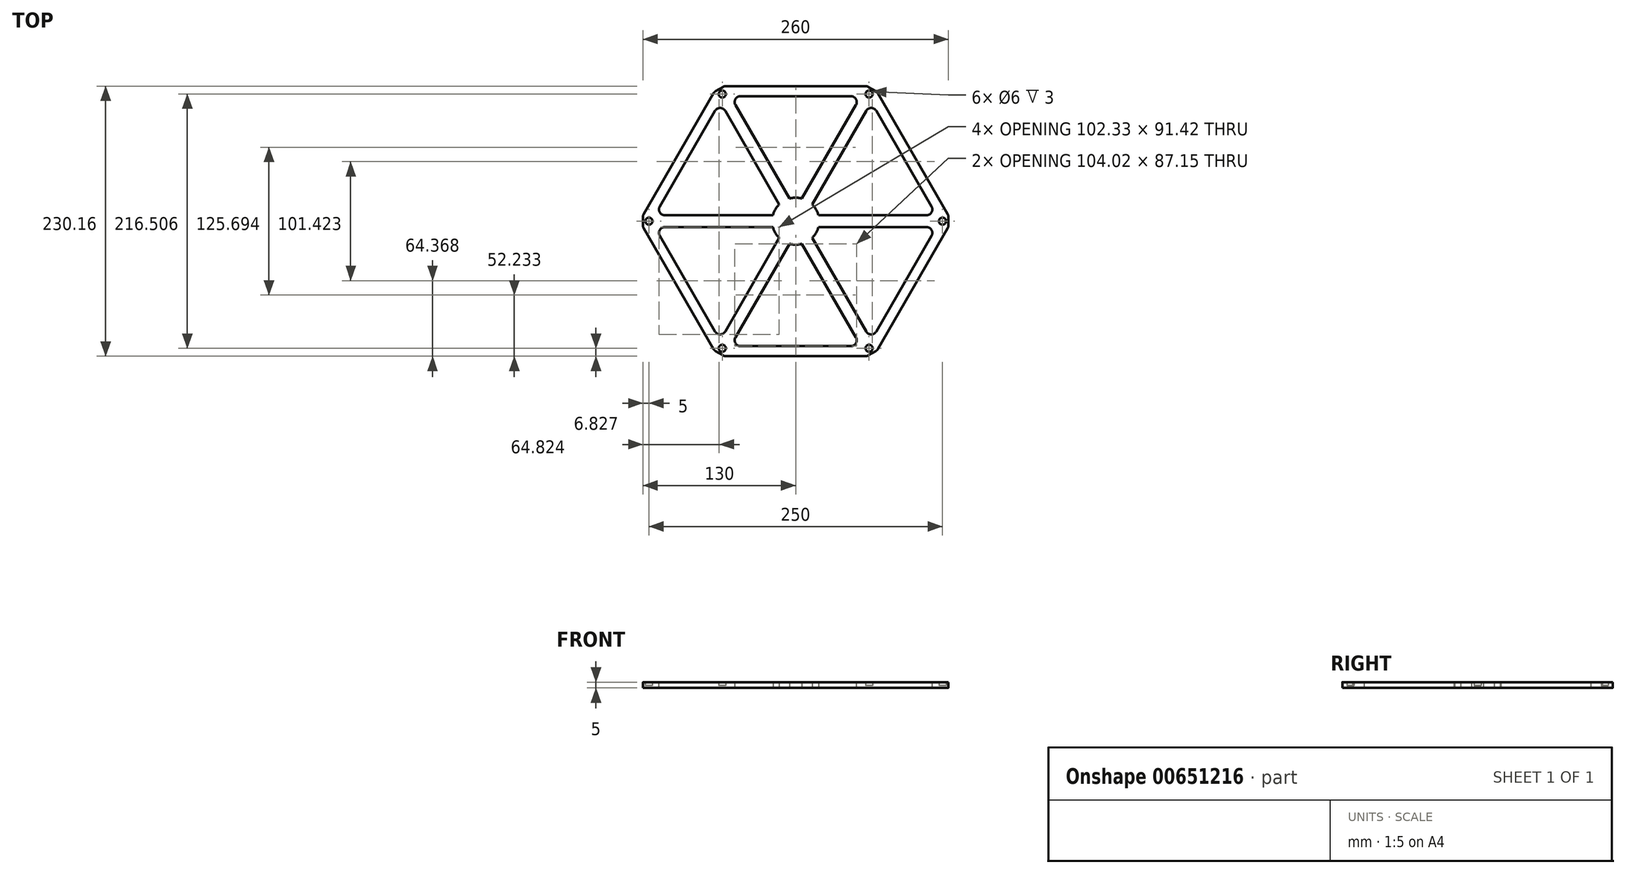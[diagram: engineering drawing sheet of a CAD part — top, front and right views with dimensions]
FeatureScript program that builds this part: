
annotation { "Feature Type Name" : "Feature", "Feature Type Description" : "" }
export const myFeature = defineFeature(function(context is Context, id is Id, definition is map)
    precondition{}
    {
        {
            var Q0;
            Q0=qCreatedBy(makeId("Top.planeOp"),FACE);
            var sketch = newSketch(context, id + "F0", { "sketchPlane" : qUnion([Q0])});
            skCircle(sketch, "E0", {"center": v(0, 0) * mm, "radius": 20 * mm});
            skLineSegment(sketch, "E1", {"start": v(-20, 0) * mm, "end": v(20, 0) * mm, "construction": true});
            skLineSegment(sketch, "E2", {"start": v(0, 0) * mm, "end": v(-10, 17.32) * mm, "construction": true});
            skLineSegment(sketch, "E3", {"start": v(0, 0) * mm, "end": v(10, 17.32) * mm, "construction": true});
            skLineSegment(sketch, "E4", {"start": v(0, 0) * mm, "end": v(-10, -17.32) * mm, "construction": true});
            skLineSegment(sketch, "E5", {"start": v(0, 0) * mm, "end": v(10, -17.32) * mm, "construction": true});
            skLineSegment(sketch, "E6", {"start": v(-20, 0) * mm, "end": v(-120, 0) * mm, "construction": true});
            skLineSegment(sketch, "E7", {"start": v(-10, 17.32) * mm, "end": v(-60, 103.92) * mm, "construction": true});
            skLineSegment(sketch, "E8", {"start": v(10, 17.32) * mm, "end": v(60, 103.92) * mm, "construction": true});
            skLineSegment(sketch, "E9", {"start": v(20, 0) * mm, "end": v(120, 0) * mm, "construction": true});
            skLineSegment(sketch, "E10", {"start": v(10, -17.32) * mm, "end": v(60, -103.92) * mm, "construction": true});
            skLineSegment(sketch, "E11", {"start": v(-10, -17.32) * mm, "end": v(-60, -103.92) * mm, "construction": true});
            skLineSegment(sketch, "E12", {"start": v(-120, 5) * mm, "end": v(-19.36, 5) * mm});
            skLineSegment(sketch, "E13", {"start": v(-120, -5) * mm, "end": v(-19.36, -5) * mm});
            skLineSegment(sketch, "E14.1.1", {"start": v(-64.33, -101.42) * mm, "end": v(-14.01, -14.27) * mm});
            skLineSegment(sketch, "E14.1.2", {"start": v(-55.67, -106.42) * mm, "end": v(-5.35, -19.27) * mm});
            skLineSegment(sketch, "E14.2.1", {"start": v(55.67, -106.42) * mm, "end": v(5.35, -19.27) * mm});
            skLineSegment(sketch, "E14.2.2", {"start": v(64.33, -101.42) * mm, "end": v(14.01, -14.27) * mm});
            skLineSegment(sketch, "E14.3.1", {"start": v(120, -5) * mm, "end": v(19.36, -5) * mm});
            skLineSegment(sketch, "E14.3.2", {"start": v(120, 5) * mm, "end": v(19.36, 5) * mm});
            skLineSegment(sketch, "E14.4.1", {"start": v(64.33, 101.42) * mm, "end": v(14.01, 14.27) * mm});
            skLineSegment(sketch, "E14.4.2", {"start": v(55.67, 106.42) * mm, "end": v(5.35, 19.27) * mm});
            skLineSegment(sketch, "E14.5.1", {"start": v(-55.67, 106.42) * mm, "end": v(-5.35, 19.27) * mm});
            skLineSegment(sketch, "E14.5.2", {"start": v(-64.33, 101.42) * mm, "end": v(-14.01, 14.27) * mm});
            skLineSegment(sketch, "E15", {"start": v(-64.33, 101.42) * mm, "end": v(-60, 103.92) * mm});
            skLineSegment(sketch, "E16", {"start": v(-55.67, 106.42) * mm, "end": v(-60, 103.92) * mm});
            skLineSegment(sketch, "E17", {"start": v(55.67, 106.42) * mm, "end": v(60, 103.92) * mm});
            skLineSegment(sketch, "E18", {"start": v(64.33, 101.42) * mm, "end": v(60, 103.92) * mm});
            skLineSegment(sketch, "E19", {"start": v(120, 5) * mm, "end": v(120, -5) * mm});
            skLineSegment(sketch, "E20", {"start": v(64.33, -101.42) * mm, "end": v(55.67, -106.42) * mm});
            skLineSegment(sketch, "E21", {"start": v(-55.67, -106.42) * mm, "end": v(-64.33, -101.42) * mm});
            skLineSegment(sketch, "E22", {"start": v(-120, -5) * mm, "end": v(-120, 5) * mm});
            skLineSegment(sketch, "E23", {"start": v(-64.33, 101.42) * mm, "end": v(-120, 5) * mm});
            skLineSegment(sketch, "E24", {"start": v(-120, -5) * mm, "end": v(-64.33, -101.42) * mm});
            skLineSegment(sketch, "E25", {"start": v(-55.67, -106.42) * mm, "end": v(55.67, -106.42) * mm});
            skLineSegment(sketch, "E26", {"start": v(64.33, -101.42) * mm, "end": v(120, -5) * mm});
            skLineSegment(sketch, "E27", {"start": v(64.33, 101.42) * mm, "end": v(120, 5) * mm});
            skLineSegment(sketch, "E28", {"start": v(-55.67, 106.42) * mm, "end": v(55.67, 106.42) * mm});
            skLineSegment(sketch, "E29", {"start": v(-120, 0) * mm, "end": v(-130, 0) * mm, "construction": true});
            skLineSegment(sketch, "E30", {"start": v(-60, 103.92) * mm, "end": v(-65, 112.58) * mm, "construction": true});
            skLineSegment(sketch, "E31", {"start": v(60, 103.92) * mm, "end": v(65, 112.58) * mm, "construction": true});
            skLineSegment(sketch, "E32", {"start": v(120, 0) * mm, "end": v(130, 0) * mm, "construction": true});
            skLineSegment(sketch, "E33", {"start": v(60, -103.92) * mm, "end": v(65.05, -112.56) * mm, "construction": true});
            skLineSegment(sketch, "E34", {"start": v(-60, -103.92) * mm, "end": v(-65, -112.58) * mm, "construction": true});
            skLineSegment(sketch, "E35", {"start": v(-65, 112.58) * mm, "end": v(-60.67, 115.08) * mm});
            skLineSegment(sketch, "E36", {"start": v(-65, 112.58) * mm, "end": v(-69.33, 110.08) * mm});
            skLineSegment(sketch, "E37.1.0", {"start": v(-130, 0) * mm, "end": v(-130, -5) * mm});
            skLineSegment(sketch, "E37.1.1", {"start": v(-130, 0) * mm, "end": v(-130, 5) * mm});
            skLineSegment(sketch, "E37.2.0", {"start": v(-65, -112.58) * mm, "end": v(-60.67, -115.08) * mm});
            skLineSegment(sketch, "E37.2.1", {"start": v(-65, -112.58) * mm, "end": v(-69.33, -110.08) * mm});
            skLineSegment(sketch, "E37.3.0", {"start": v(65, -112.58) * mm, "end": v(69.33, -110.08) * mm});
            skLineSegment(sketch, "E37.3.1", {"start": v(65, -112.58) * mm, "end": v(60.67, -115.08) * mm});
            skLineSegment(sketch, "E37.4.0", {"start": v(130, 0) * mm, "end": v(130, 5) * mm});
            skLineSegment(sketch, "E37.4.1", {"start": v(130, 0) * mm, "end": v(130, -5) * mm});
            skLineSegment(sketch, "E37.5.0", {"start": v(65, 112.58) * mm, "end": v(60.67, 115.08) * mm});
            skLineSegment(sketch, "E37.5.1", {"start": v(65, 112.58) * mm, "end": v(69.33, 110.08) * mm});
            skLineSegment(sketch, "E38", {"start": v(-69.33, 110.08) * mm, "end": v(-130, 5) * mm});
            skLineSegment(sketch, "E39", {"start": v(-130, -5) * mm, "end": v(-69.33, -110.08) * mm});
            skLineSegment(sketch, "E40", {"start": v(-60.67, -115.08) * mm, "end": v(60.67, -115.08) * mm});
            skLineSegment(sketch, "E41", {"start": v(69.33, -110.08) * mm, "end": v(130, -5) * mm});
            skLineSegment(sketch, "E42", {"start": v(130, 5) * mm, "end": v(69.33, 110.08) * mm});
            skLineSegment(sketch, "E43", {"start": v(60.67, 115.08) * mm, "end": v(-60.67, 115.08) * mm});
            skLineSegment(sketch, "E44", {"start": v(60.67, 115.08) * mm, "end": v(64.33, 101.42) * mm, "construction": true});
            skLineSegment(sketch, "E45", {"start": v(55.67, 106.42) * mm, "end": v(69.33, 110.08) * mm, "construction": true});
            skPoint(sketch, "E46", {"position": v(62.5, 108.25) * mm});
            skCircle(sketch, "E47", {"center": v(62.5, 108.25) * mm, "radius": 3 * mm});
            skCircle(sketch, "E48.1.0", {"center": v(-62.5, 108.25) * mm, "radius": 3 * mm});
            skCircle(sketch, "E48.2.0", {"center": v(-125, 0) * mm, "radius": 3 * mm});
            skCircle(sketch, "E48.3.0", {"center": v(-62.5, -108.25) * mm, "radius": 3 * mm});
            skCircle(sketch, "E48.4.0", {"center": v(62.5, -108.25) * mm, "radius": 3 * mm});
            skCircle(sketch, "E48.5.0", {"center": v(125, 0) * mm, "radius": 3 * mm});
            skSolve(sketch);
        }
        {
            var Q0;
            Q0=makeQuery(id+"F0.imprint","IMPRINT",FACE,{"disambiguationData":[TD([[makeQuery(id+"F0.imprint","IMPRINT",EDGE,{"derivedFrom":sQuery(id+"F0.wireOp",EDGE,"E15")}),1.0]])]});
            extrude(context, id + "F1", {"entities" : qUnion([Q0]), "depth" : 5 * mm, "offsetDistance" : 25 * mm});
        }
        {
            var Q0;
            {var subQ0=sQuery(id+"F0.wireOp",EDGE,"E0");var subQ8=makeQuery(id+"F0.imprint","INTERSECT",VERTEX,{"derivedFrom":[subQ0,sQuery(id+"F0.wireOp",EDGE,"E14.3.2")]});Q0=makeQuery(id+"F0.imprint","IMPRINT",FACE,{"disambiguationData":[TD([[makeQuery(id+"F0.imprint","IMPRINT",EDGE,{"disambiguationData":[TD([[subQ8,-1.0]])],"derivedFrom":subQ0}),1.0]])]});}
            var Q1;
            {var subQ0=sQuery(id+"F0.wireOp",EDGE,"E12");Q1=makeQuery(id+"F0.imprint","IMPRINT",FACE,{"disambiguationData":[TD([[makeQuery(id+"F0.imprint","IMPRINT",EDGE,{"derivedFrom":subQ0}),-1.0]])]});}
            var Q2;
            {var subQ0=sQuery(id+"F0.wireOp",EDGE,"E14.5.1");Q2=makeQuery(id+"F0.imprint","IMPRINT",FACE,{"disambiguationData":[TD([[makeQuery(id+"F0.imprint","IMPRINT",EDGE,{"derivedFrom":subQ0}),-1.0]])]});}
            var Q3;
            {var subQ0=sQuery(id+"F0.wireOp",EDGE,"E14.4.1");Q3=makeQuery(id+"F0.imprint","IMPRINT",FACE,{"disambiguationData":[TD([[makeQuery(id+"F0.imprint","IMPRINT",EDGE,{"derivedFrom":subQ0}),-1.0]])]});}
            var Q4;
            {var subQ0=sQuery(id+"F0.wireOp",EDGE,"E14.3.1");Q4=makeQuery(id+"F0.imprint","IMPRINT",FACE,{"disambiguationData":[TD([[makeQuery(id+"F0.imprint","IMPRINT",EDGE,{"derivedFrom":subQ0}),-1.0]])]});}
            var Q5;
            {var subQ0=sQuery(id+"F0.wireOp",EDGE,"E14.2.1");Q5=makeQuery(id+"F0.imprint","IMPRINT",FACE,{"disambiguationData":[TD([[makeQuery(id+"F0.imprint","IMPRINT",EDGE,{"derivedFrom":subQ0}),-1.0]])]});}
            var Q6;
            {var subQ0=sQuery(id+"F0.wireOp",EDGE,"E14.1.1");Q6=makeQuery(id+"F0.imprint","IMPRINT",FACE,{"disambiguationData":[TD([[makeQuery(id+"F0.imprint","IMPRINT",EDGE,{"derivedFrom":subQ0}),-1.0]])]});}
            extrude(context, id + "F2", {"entities" : qUnion([Q0, Q1, Q2, Q3, Q4, Q5, Q6]), "operationType" : NewBodyOperationType.ADD, "depth" : 5 * mm, "offsetDistance" : 25 * mm});
        }
        {
            var Q0;
            Q0=makeQuery(id+"F1.opExtrude","SWEPT_EDGE",EDGE,{"disambiguationData":[OSD([sQuery(id+"F0.wireOp",EDGE,"E37.2.0"),sQuery(id+"F0.wireOp",EDGE,"E40")])]});
            fillet(context, id + "F3", {"entities" : qUnion([Q0]), "radius" : 5 * mm, "tangentPropagation" : true, "allowEdgeOverflow" : false});
        }
        {
            var Q0;
            Q0=makeQuery(id+"F1.opExtrude","SWEPT_EDGE",EDGE,{"disambiguationData":[OSD([sQuery(id+"F0.wireOp",EDGE,"E37.2.1"),sQuery(id+"F0.wireOp",EDGE,"E39")])]});
            var Q1;
            Q1=makeQuery(id+"F1.opExtrude","SWEPT_EDGE",EDGE,{"disambiguationData":[OSD([sQuery(id+"F0.wireOp",EDGE,"E37.3.1"),sQuery(id+"F0.wireOp",EDGE,"E40")])]});
            var Q2;
            Q2=makeQuery(id+"F1.opExtrude","SWEPT_EDGE",EDGE,{"disambiguationData":[OSD([sQuery(id+"F0.wireOp",EDGE,"E37.3.0"),sQuery(id+"F0.wireOp",EDGE,"E41")])]});
            var Q3;
            Q3=makeQuery(id+"F1.opExtrude","SWEPT_EDGE",EDGE,{"disambiguationData":[OSD([sQuery(id+"F0.wireOp",EDGE,"E37.4.1"),sQuery(id+"F0.wireOp",EDGE,"E41")])]});
            var Q4;
            Q4=makeQuery(id+"F1.opExtrude","SWEPT_EDGE",EDGE,{"disambiguationData":[OSD([sQuery(id+"F0.wireOp",EDGE,"E37.4.0"),sQuery(id+"F0.wireOp",EDGE,"E42")])]});
            var Q5;
            Q5=makeQuery(id+"F1.opExtrude","SWEPT_EDGE",EDGE,{"disambiguationData":[OSD([sQuery(id+"F0.wireOp",EDGE,"E37.5.1"),sQuery(id+"F0.wireOp",EDGE,"E42")])]});
            var Q6;
            Q6=makeQuery(id+"F1.opExtrude","SWEPT_EDGE",EDGE,{"disambiguationData":[OSD([sQuery(id+"F0.wireOp",EDGE,"E37.5.0"),sQuery(id+"F0.wireOp",EDGE,"E43")])]});
            var Q7;
            Q7=makeQuery(id+"F1.opExtrude","SWEPT_EDGE",EDGE,{"disambiguationData":[OSD([sQuery(id+"F0.wireOp",EDGE,"E35"),sQuery(id+"F0.wireOp",EDGE,"E43")])]});
            var Q8;
            Q8=makeQuery(id+"F1.opExtrude","SWEPT_EDGE",EDGE,{"disambiguationData":[OSD([sQuery(id+"F0.wireOp",EDGE,"E36"),sQuery(id+"F0.wireOp",EDGE,"E38")])]});
            var Q9;
            Q9=makeQuery(id+"F1.opExtrude","SWEPT_EDGE",EDGE,{"disambiguationData":[OSD([sQuery(id+"F0.wireOp",EDGE,"E37.1.1"),sQuery(id+"F0.wireOp",EDGE,"E38")])]});
            var Q10;
            Q10=makeQuery(id+"F1.opExtrude","SWEPT_EDGE",EDGE,{"disambiguationData":[OSD([sQuery(id+"F0.wireOp",EDGE,"E37.1.0"),sQuery(id+"F0.wireOp",EDGE,"E39")])]});
            fillet(context, id + "F4", {"entities" : qUnion([Q0, Q1, Q2, Q3, Q4, Q5, Q6, Q7, Q8, Q9, Q10]), "radius" : 5 * mm, "tangentPropagation" : true, "allowEdgeOverflow" : false});
        }
        {
            var Q0;
            Q0=makeQuery(id+"F0.imprint","IMPRINT",FACE,{"disambiguationData":[TD([[makeQuery(id+"F0.imprint","IMPRINT",EDGE,{"derivedFrom":sQuery(id+"F0.wireOp",EDGE,"E48.2.0")}),1.0]])]});
            extrude(context, id + "F5", {"entities" : qUnion([Q0]), "operationType" : NewBodyOperationType.ADD, "depth" : 2 * mm, "offsetDistance" : 25 * mm});
        }
        {
            var Q0;
            Q0=makeQuery(id+"F0.imprint","IMPRINT",FACE,{"disambiguationData":[TD([[makeQuery(id+"F0.imprint","IMPRINT",EDGE,{"derivedFrom":sQuery(id+"F0.wireOp",EDGE,"E48.1.0")}),1.0]])]});
            extrude(context, id + "F6", {"entities" : qUnion([Q0]), "operationType" : NewBodyOperationType.ADD, "depth" : 2 * mm, "offsetDistance" : 25 * mm});
        }
        {
            var Q0;
            Q0=makeQuery(id+"F0.imprint","IMPRINT",FACE,{"disambiguationData":[TD([[makeQuery(id+"F0.imprint","IMPRINT",EDGE,{"derivedFrom":sQuery(id+"F0.wireOp",EDGE,"E47")}),1.0]])]});
            extrude(context, id + "F7", {"entities" : qUnion([Q0]), "operationType" : NewBodyOperationType.ADD, "depth" : 2 * mm, "offsetDistance" : 25 * mm});
        }
        {
            var Q0;
            Q0=makeQuery(id+"F0.imprint","IMPRINT",FACE,{"disambiguationData":[TD([[makeQuery(id+"F0.imprint","IMPRINT",EDGE,{"derivedFrom":sQuery(id+"F0.wireOp",EDGE,"E48.5.0")}),1.0]])]});
            extrude(context, id + "F8", {"entities" : qUnion([Q0]), "operationType" : NewBodyOperationType.ADD, "depth" : 2 * mm, "offsetDistance" : 25 * mm});
        }
        {
            var Q0;
            Q0=makeQuery(id+"F0.imprint","IMPRINT",FACE,{"disambiguationData":[TD([[makeQuery(id+"F0.imprint","IMPRINT",EDGE,{"derivedFrom":sQuery(id+"F0.wireOp",EDGE,"E48.4.0")}),1.0]])]});
            extrude(context, id + "F9", {"entities" : qUnion([Q0]), "operationType" : NewBodyOperationType.ADD, "depth" : 2 * mm, "offsetDistance" : 25 * mm});
        }
        {
            var Q0;
            Q0=makeQuery(id+"F0.imprint","IMPRINT",FACE,{"disambiguationData":[TD([[makeQuery(id+"F0.imprint","IMPRINT",EDGE,{"derivedFrom":sQuery(id+"F0.wireOp",EDGE,"E48.3.0")}),1.0]])]});
            extrude(context, id + "F10", {"entities" : qUnion([Q0]), "operationType" : NewBodyOperationType.ADD, "depth" : 2 * mm, "offsetDistance" : 25 * mm});
        }
        {
            var Q0;
            {var subQ0=sQuery(id+"F0.wireOp",EDGE,"E24");var subQ1=sQuery(id+"F0.wireOp",EDGE,"E21");var subQ2=sQuery(id+"F0.wireOp",EDGE,"E14.1.1");Q0=makeQuery(id+"F2.boolean.opBoolean","MERGE",EDGE,{"derivedFrom":[makeQuery(id+"F1.opExtrude","SWEPT_EDGE",EDGE,{"disambiguationData":[OSD([subQ2,subQ1,subQ0])]}),makeQuery(id+"F2.opExtrude","SWEPT_EDGE",EDGE,{"disambiguationData":[OSD([subQ2,subQ1,subQ0])]})]});}
            var Q1;
            {var subQ0=sQuery(id+"F0.wireOp",EDGE,"E24");var subQ1=sQuery(id+"F0.wireOp",EDGE,"E22");var subQ2=sQuery(id+"F0.wireOp",EDGE,"E13");Q1=makeQuery(id+"F2.boolean.opBoolean","MERGE",EDGE,{"derivedFrom":[makeQuery(id+"F1.opExtrude","SWEPT_EDGE",EDGE,{"disambiguationData":[OSD([subQ2,subQ1,subQ0])]}),makeQuery(id+"F2.opExtrude","SWEPT_EDGE",EDGE,{"disambiguationData":[OSD([subQ2,subQ1,subQ0])]})]});}
            var Q2;
            {var subQ0=sQuery(id+"F0.wireOp",EDGE,"E23");var subQ1=sQuery(id+"F0.wireOp",EDGE,"E22");var subQ2=sQuery(id+"F0.wireOp",EDGE,"E12");Q2=makeQuery(id+"F2.boolean.opBoolean","MERGE",EDGE,{"derivedFrom":[makeQuery(id+"F1.opExtrude","SWEPT_EDGE",EDGE,{"disambiguationData":[OSD([subQ2,subQ1,subQ0])]}),makeQuery(id+"F2.opExtrude","SWEPT_EDGE",EDGE,{"disambiguationData":[OSD([subQ2,subQ1,subQ0])]})]});}
            var Q3;
            {var subQ0=sQuery(id+"F0.wireOp",EDGE,"E23");var subQ1=sQuery(id+"F0.wireOp",EDGE,"E15");var subQ2=sQuery(id+"F0.wireOp",EDGE,"E14.5.2");Q3=makeQuery(id+"F2.boolean.opBoolean","MERGE",EDGE,{"derivedFrom":[makeQuery(id+"F1.opExtrude","SWEPT_EDGE",EDGE,{"disambiguationData":[OSD([subQ2,subQ1,subQ0])]}),makeQuery(id+"F2.opExtrude","SWEPT_EDGE",EDGE,{"disambiguationData":[OSD([subQ2,subQ1,subQ0])]})]});}
            var Q4;
            {var subQ0=sQuery(id+"F0.wireOp",EDGE,"E28");var subQ1=sQuery(id+"F0.wireOp",EDGE,"E16");var subQ2=sQuery(id+"F0.wireOp",EDGE,"E14.5.1");Q4=makeQuery(id+"F2.boolean.opBoolean","MERGE",EDGE,{"derivedFrom":[makeQuery(id+"F1.opExtrude","SWEPT_EDGE",EDGE,{"disambiguationData":[OSD([subQ2,subQ1,subQ0])]}),makeQuery(id+"F2.opExtrude","SWEPT_EDGE",EDGE,{"disambiguationData":[OSD([subQ2,subQ1,subQ0])]})]});}
            var Q5;
            {var subQ0=sQuery(id+"F0.wireOp",EDGE,"E28");var subQ1=sQuery(id+"F0.wireOp",EDGE,"E17");var subQ2=sQuery(id+"F0.wireOp",EDGE,"E14.4.2");Q5=makeQuery(id+"F2.boolean.opBoolean","MERGE",EDGE,{"derivedFrom":[makeQuery(id+"F1.opExtrude","SWEPT_EDGE",EDGE,{"disambiguationData":[OSD([subQ2,subQ1,subQ0])]}),makeQuery(id+"F2.opExtrude","SWEPT_EDGE",EDGE,{"disambiguationData":[OSD([subQ2,subQ1,subQ0])]})]});}
            var Q6;
            {var subQ0=sQuery(id+"F0.wireOp",EDGE,"E27");var subQ1=sQuery(id+"F0.wireOp",EDGE,"E18");var subQ2=sQuery(id+"F0.wireOp",EDGE,"E14.4.1");Q6=makeQuery(id+"F2.boolean.opBoolean","MERGE",EDGE,{"derivedFrom":[makeQuery(id+"F1.opExtrude","SWEPT_EDGE",EDGE,{"disambiguationData":[OSD([subQ2,subQ1,subQ0])]}),makeQuery(id+"F2.opExtrude","SWEPT_EDGE",EDGE,{"disambiguationData":[OSD([subQ2,subQ1,subQ0])]})]});}
            var Q7;
            {var subQ0=sQuery(id+"F0.wireOp",EDGE,"E27");var subQ1=sQuery(id+"F0.wireOp",EDGE,"E19");var subQ2=sQuery(id+"F0.wireOp",EDGE,"E14.3.2");Q7=makeQuery(id+"F2.boolean.opBoolean","MERGE",EDGE,{"derivedFrom":[makeQuery(id+"F1.opExtrude","SWEPT_EDGE",EDGE,{"disambiguationData":[OSD([subQ2,subQ1,subQ0])]}),makeQuery(id+"F2.opExtrude","SWEPT_EDGE",EDGE,{"disambiguationData":[OSD([subQ2,subQ1,subQ0])]})]});}
            var Q8;
            {var subQ0=sQuery(id+"F0.wireOp",EDGE,"E26");var subQ1=sQuery(id+"F0.wireOp",EDGE,"E19");var subQ2=sQuery(id+"F0.wireOp",EDGE,"E14.3.1");Q8=makeQuery(id+"F2.boolean.opBoolean","MERGE",EDGE,{"derivedFrom":[makeQuery(id+"F1.opExtrude","SWEPT_EDGE",EDGE,{"disambiguationData":[OSD([subQ2,subQ1,subQ0])]}),makeQuery(id+"F2.opExtrude","SWEPT_EDGE",EDGE,{"disambiguationData":[OSD([subQ2,subQ1,subQ0])]})]});}
            var Q9;
            {var subQ0=sQuery(id+"F0.wireOp",EDGE,"E26");var subQ1=sQuery(id+"F0.wireOp",EDGE,"E20");var subQ2=sQuery(id+"F0.wireOp",EDGE,"E14.2.2");Q9=makeQuery(id+"F2.boolean.opBoolean","MERGE",EDGE,{"derivedFrom":[makeQuery(id+"F1.opExtrude","SWEPT_EDGE",EDGE,{"disambiguationData":[OSD([subQ2,subQ1,subQ0])]}),makeQuery(id+"F2.opExtrude","SWEPT_EDGE",EDGE,{"disambiguationData":[OSD([subQ2,subQ1,subQ0])]})]});}
            var Q10;
            {var subQ0=sQuery(id+"F0.wireOp",EDGE,"E25");var subQ1=sQuery(id+"F0.wireOp",EDGE,"E20");var subQ2=sQuery(id+"F0.wireOp",EDGE,"E14.2.1");Q10=makeQuery(id+"F2.boolean.opBoolean","MERGE",EDGE,{"derivedFrom":[makeQuery(id+"F1.opExtrude","SWEPT_EDGE",EDGE,{"disambiguationData":[OSD([subQ2,subQ1,subQ0])]}),makeQuery(id+"F2.opExtrude","SWEPT_EDGE",EDGE,{"disambiguationData":[OSD([subQ2,subQ1,subQ0])]})]});}
            var Q11;
            {var subQ0=sQuery(id+"F0.wireOp",EDGE,"E25");var subQ1=sQuery(id+"F0.wireOp",EDGE,"E21");var subQ2=sQuery(id+"F0.wireOp",EDGE,"E14.1.2");Q11=makeQuery(id+"F2.boolean.opBoolean","MERGE",EDGE,{"derivedFrom":[makeQuery(id+"F1.opExtrude","SWEPT_EDGE",EDGE,{"disambiguationData":[OSD([subQ2,subQ1,subQ0])]}),makeQuery(id+"F2.opExtrude","SWEPT_EDGE",EDGE,{"disambiguationData":[OSD([subQ2,subQ1,subQ0])]})]});}
            fillet(context, id + "F11", {"entities" : qUnion([Q0, Q1, Q2, Q3, Q4, Q5, Q6, Q7, Q8, Q9, Q10, Q11]), "radius" : 5 * mm, "tangentPropagation" : true, "allowEdgeOverflow" : false});
        }
    });
